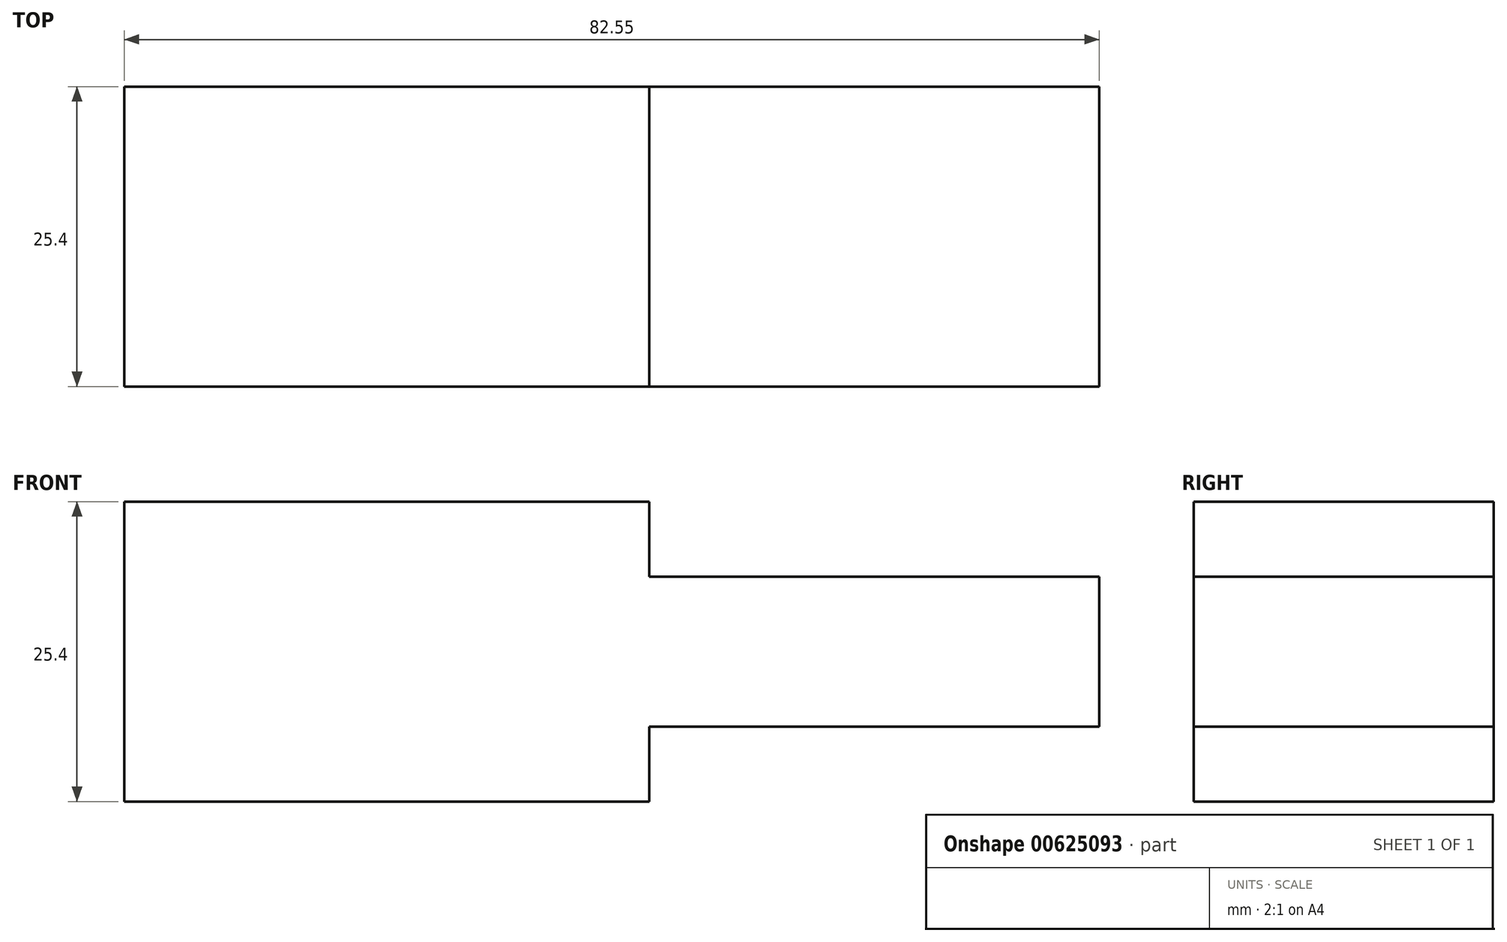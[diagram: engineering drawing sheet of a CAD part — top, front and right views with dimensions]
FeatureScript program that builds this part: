
annotation { "Feature Type Name" : "Feature", "Feature Type Description" : "" }
export const myFeature = defineFeature(function(context is Context, id is Id, definition is map)
    precondition{}
    {
        {
            var Q0;
            Q0=qCreatedBy(makeId("Front.planeOp"),FACE);
            var sketch = newSketch(context, id + "F0", { "sketchPlane" : qUnion([Q0])});
            skLineSegment(sketch, "E0", {"start": v(0, 0) * mm, "end": v(44.45, 0) * mm});
            skLineSegment(sketch, "E1", {"start": v(44.45, 0) * mm, "end": v(44.45, 6.35) * mm});
            skLineSegment(sketch, "E2", {"start": v(44.45, 6.35) * mm, "end": v(82.55, 6.35) * mm});
            skLineSegment(sketch, "E3", {"start": v(82.55, 6.35) * mm, "end": v(82.55, 19.05) * mm});
            skLineSegment(sketch, "E4", {"start": v(82.55, 19.05) * mm, "end": v(44.45, 19.05) * mm});
            skLineSegment(sketch, "E5", {"start": v(44.45, 19.05) * mm, "end": v(44.45, 25.4) * mm});
            skLineSegment(sketch, "E6", {"start": v(44.45, 25.4) * mm, "end": v(0, 25.4) * mm});
            skLineSegment(sketch, "E7", {"start": v(0, 25.4) * mm, "end": v(0, 0) * mm});
            skSolve(sketch);
        }
        {
            var Q0;
            Q0 = qSketchRegion(id + "F0", true);
            extrude(context, id + "F1", {"entities" : qUnion([Q0]), "depth" : 25.4 * mm, "offsetDistance" : 25.4 * mm});
        }
    });
